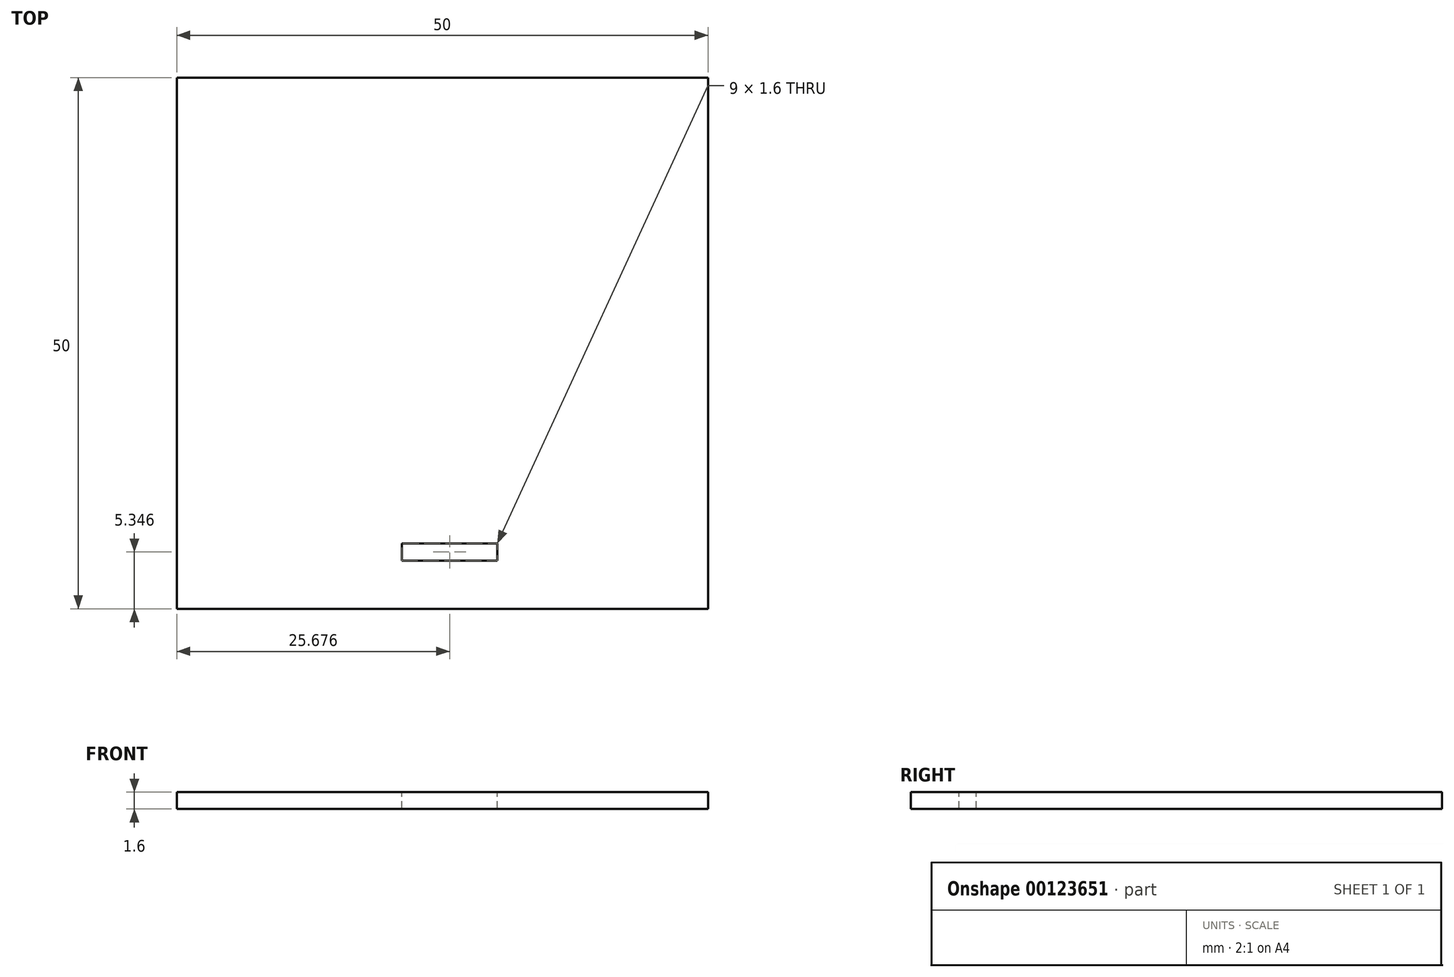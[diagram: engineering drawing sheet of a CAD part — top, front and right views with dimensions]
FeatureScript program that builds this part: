
annotation { "Feature Type Name" : "Feature", "Feature Type Description" : "" }
export const myFeature = defineFeature(function(context is Context, id is Id, definition is map)
    precondition{}
    {
        {
            var Q0;
            Q0=qCreatedBy(makeId("Top.planeOp"),FACE);
            var sketch = newSketch(context, id + "F0", { "sketchPlane" : qUnion([Q0])});
            skLineSegment(sketch, "E0.bottom", {"start": v(0, 0) * mm, "end": v(50, 0) * mm});
            skLineSegment(sketch, "E0.top", {"start": v(0, 50) * mm, "end": v(50, 50) * mm});
            skLineSegment(sketch, "E0.left", {"start": v(0, 0) * mm, "end": v(0, 50) * mm});
            skLineSegment(sketch, "E0.right", {"start": v(50, 0) * mm, "end": v(50, 50) * mm});
            skSolve(sketch);
        }
        {
            var Q0;
            Q0=makeQuery(id+"F0.imprint","IMPRINT",FACE,{"disambiguationData":[TD([[makeQuery(id+"F0.imprint","IMPRINT",EDGE,{"derivedFrom":sQuery(id+"F0.wireOp",EDGE,"E0.bottom")}),1.0]])]});
            extrude(context, id + "F1", {"entities" : qUnion([Q0]), "depth" : 1.6 * mm});
        }
        {
            var Q0;
            Q0=makeQuery(id+"F1.opExtrude","CAP_FACE",FACE,{"disambiguationData":[OSD([sQuery(id+"F0.wireOp",EDGE,"E0.bottom"),sQuery(id+"F0.wireOp",EDGE,"E0.top"),sQuery(id+"F0.wireOp",EDGE,"E0.left"),sQuery(id+"F0.wireOp",EDGE,"E0.right")])],"isStart":false});
            var sketch = newSketch(context, id + "F2", { "sketchPlane" : qUnion([Q0])});
            skLineSegment(sketch, "E1.bottom", {"start": v(21.18, 6.15) * mm, "end": v(30.18, 6.15) * mm});
            skLineSegment(sketch, "E1.top", {"start": v(21.18, 4.55) * mm, "end": v(30.18, 4.55) * mm});
            skLineSegment(sketch, "E1.left", {"start": v(21.18, 6.15) * mm, "end": v(21.18, 4.55) * mm});
            skLineSegment(sketch, "E1.right", {"start": v(30.18, 6.15) * mm, "end": v(30.18, 4.55) * mm});
            skSolve(sketch);
        }
        {
            var Q0;
            Q0 = qSketchRegion(id + "F2", true);
            extrude(context, id + "F3", {"entities" : qUnion([Q0]), "operationType" : NewBodyOperationType.REMOVE, "oppositeDirection" : true, "depth" : 25 * mm});
        }
    });
